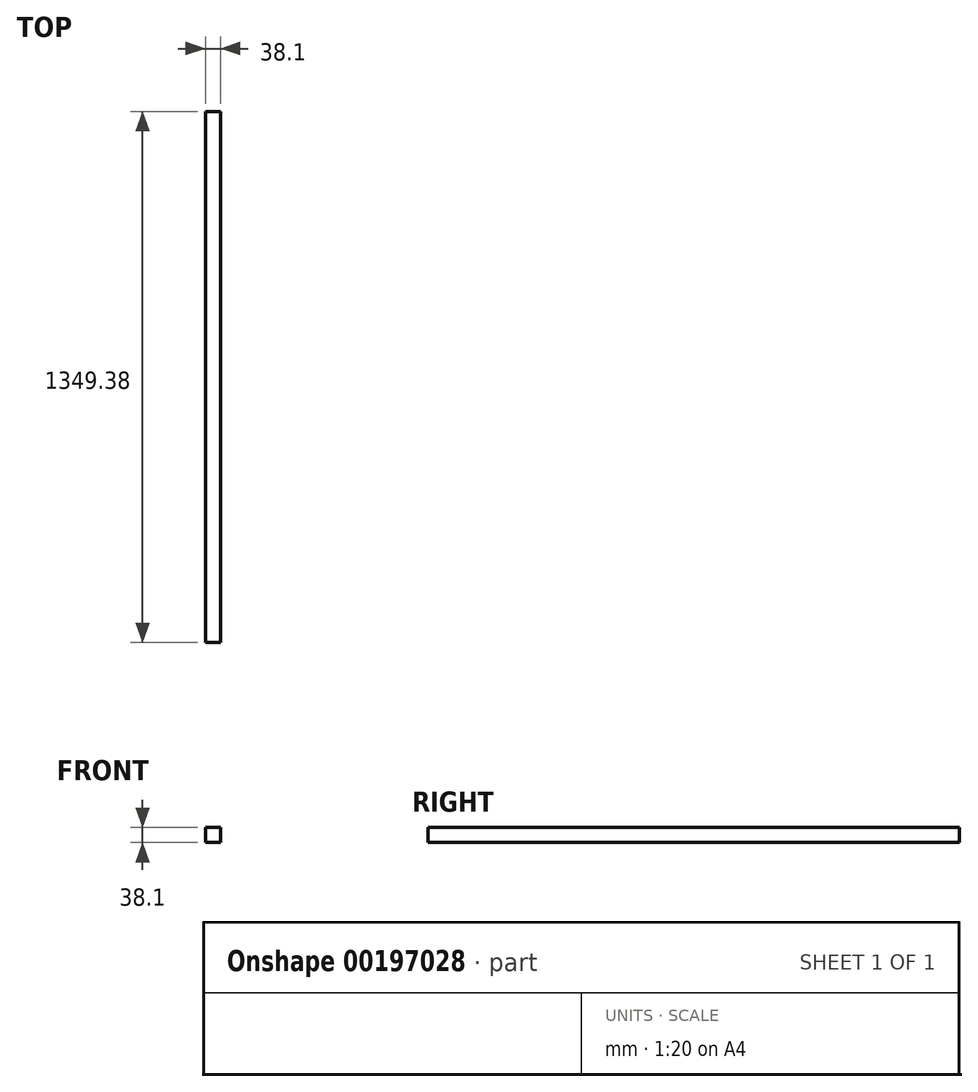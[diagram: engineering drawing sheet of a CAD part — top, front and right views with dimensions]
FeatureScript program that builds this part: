
annotation { "Feature Type Name" : "Feature", "Feature Type Description" : "" }
export const myFeature = defineFeature(function(context is Context, id is Id, definition is map)
    precondition{}
    {
        {
            var Q0;
            Q0=qCreatedBy(makeId("Front.planeOp"),FACE);
            var sketch = newSketch(context, id + "F0", { "sketchPlane" : qUnion([Q0])});
            skLineSegment(sketch, "E0.bottom", {"start": v(0, 0) * mm, "end": v(38.1, 0) * mm});
            skLineSegment(sketch, "E0.top", {"start": v(0, 38.1) * mm, "end": v(38.1, 38.1) * mm});
            skLineSegment(sketch, "E0.left", {"start": v(0, 0) * mm, "end": v(0, 38.1) * mm});
            skLineSegment(sketch, "E0.right", {"start": v(38.1, 0) * mm, "end": v(38.1, 38.1) * mm});
            skSolve(sketch);
        }
        {
            var Q0;
            Q0=makeQuery(id+"F0.imprint","IMPRINT",FACE,{"disambiguationData":[TD([[makeQuery(id+"F0.imprint","IMPRINT",EDGE,{"derivedFrom":sQuery(id+"F0.wireOp",EDGE,"E0.bottom")}),1.0]])]});
            extrude(context, id + "F1", {"entities" : qUnion([Q0]), "depth" : 1349.38 * mm});
        }
    });
